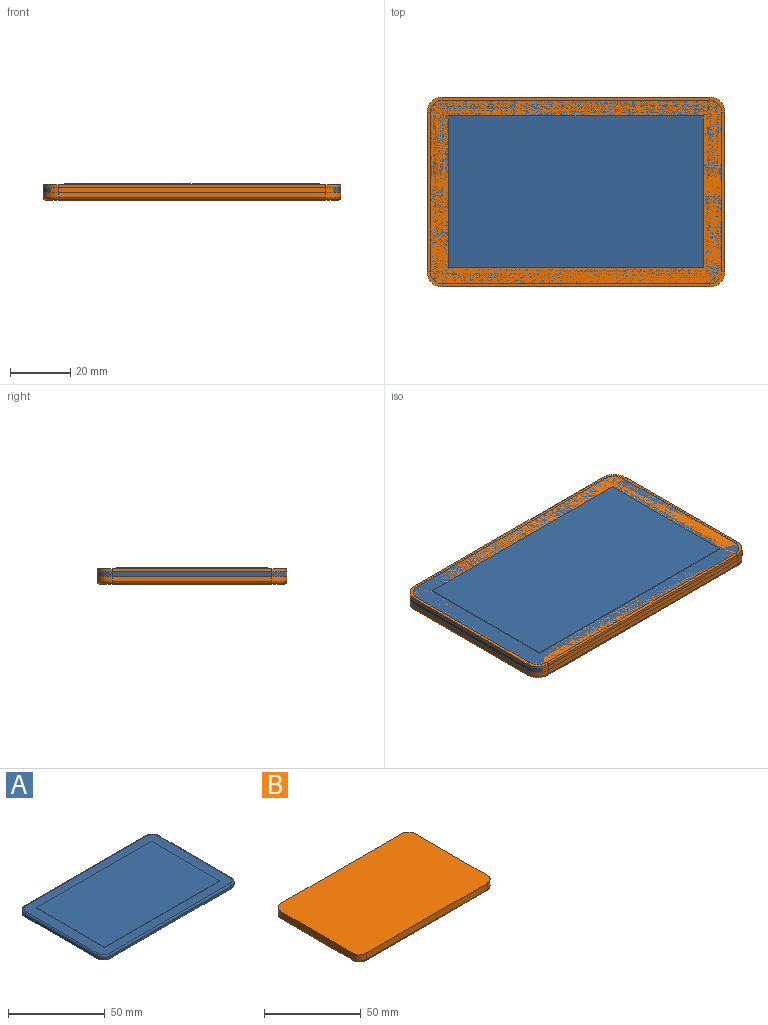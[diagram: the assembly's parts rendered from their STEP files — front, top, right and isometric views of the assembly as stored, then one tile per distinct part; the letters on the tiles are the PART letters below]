
ASSEMBLY  parts=2 mates=1
PART A: 23 faces, bbox 99.3x63.6x2.8 mm
  f0: plane 96.5x60.76mm, normal (0,0,1), area 1613.6mm2, adj f6,f7,f8,f9,f11,f13,f15,f17
  f1: plane 88.34x1.54mm, normal (0,1,0), area 136mm2, adj f5,f6,f14,f16
  f2: plane 52.6x1.54mm, normal (-1,0,0), area 81mm2, adj f5,f7,f12,f16
  f3: plane 88.34x1.54mm, normal (0,-1,0), area 136mm2, adj f5,f9,f10,f12
  f4: plane 52.6x1.54mm, normal (1,0,0), area 81mm2, adj f5,f8,f10,f14
  f5: plane 98.5x62.76mm, normal (0,0,-1), area 6160.1mm2, adj f1,f2,f3,f4,f10,f12,f14,f16
  f6: cylinder r=1mm len=88.34mm, axis (1,0,0), area 138.8mm2, adj f0,f1,f15,f17
  f7: cylinder r=1mm len=52.6mm, axis (0,1,0), area 82.6mm2, adj f0,f2,f13,f17
  f8: cylinder r=1mm len=52.6mm, axis (0,-1,0), area 82.6mm2, adj f0,f4,f11,f15
  f9: cylinder r=1mm len=88.34mm, axis (-1,0,0), area 138.8mm2, adj f0,f3,f11,f13
  f10: cylinder r=5.08mm len=5.08mm, axis (0,0,1), area 12.3mm2, adj f3,f4,f5,f11
  f11: torus R=4.08mm, axis (0,0,1), area 11.6mm2, adj f0,f8,f9,f10
  f12: cylinder r=5.08mm len=5.08mm, axis (0,0,-1), area 12.3mm2, adj f2,f3,f5,f13
  f13: torus R=4.08mm, axis (0,0,1), area 11.6mm2, adj f0,f7,f9,f12
  f14: cylinder r=5.08mm len=5.08mm, axis (0,0,-1), area 12.3mm2, adj f1,f4,f5,f15
  f15: torus R=4.08mm, axis (0,0,1), area 11.6mm2, adj f0,f6,f8,f14
  f16: cylinder r=5.08mm len=5.08mm, axis (0,0,1), area 12.3mm2, adj f1,f2,f5,f17
  f17: torus R=4.08mm, axis (0,0,1), area 11.6mm2, adj f0,f6,f7,f16
  f18: plane 84.26x0.25mm, normal (0,1,0), area 21.4mm2, adj f0,f19,f21,f22
  f19: plane 50.27x0.25mm, normal (-1,0,0), area 12.8mm2, adj f0,f18,f20,f22
  f20: plane 84.26x0.25mm, normal (0,-1,0), area 21.4mm2, adj f0,f19,f21,f22
  f21: plane 50.27x0.25mm, normal (1,0,0), area 12.8mm2, adj f0,f18,f20,f22
  f22: plane 84.26x50.27mm, normal (0,0,1), area 4235.8mm2, adj f18,f19,f20,f21
PART B: 18 faces, bbox 99.3x63.6x5.1 mm
  f0: plane 96.5x60.77mm, normal (0,0,-1), area 5849.4mm2, adj f6,f7,f8,f9,f11,f13,f15,f17
  f1: plane 88.34x4.08mm, normal (0,1,0), area 360.4mm2, adj f5,f6,f14,f16
  f2: plane 52.61x4.08mm, normal (-1,0,0), area 214.6mm2, adj f5,f7,f12,f16
  f3: plane 88.34x4.08mm, normal (0,-1,0), area 360.4mm2, adj f5,f9,f10,f12
  f4: plane 52.61x4.08mm, normal (1,0,0), area 214.6mm2, adj f5,f8,f10,f14
  f5: plane 98.5x62.77mm, normal (0,0,1), area 6160.1mm2, adj f1,f2,f3,f4,f10,f12,f14,f16
  f6: cylinder r=1mm len=88.34mm, axis (1,0,0), area 138.8mm2, adj f0,f1,f15,f17
  f7: cylinder r=1mm len=52.61mm, axis (0,1,0), area 82.6mm2, adj f0,f2,f13,f17
  f8: cylinder r=1mm len=52.61mm, axis (0,-1,0), area 82.6mm2, adj f0,f4,f11,f15
  f9: cylinder r=1mm len=88.34mm, axis (-1,0,0), area 138.8mm2, adj f0,f3,f11,f13
  f10: cylinder r=5.08mm len=5.08mm, axis (0,0,-1), area 32.6mm2, adj f3,f4,f5,f11
  f11: torus R=4.08mm, axis (0,0,1), area 11.6mm2, adj f0,f8,f9,f10
  f12: cylinder r=5.08mm len=5.08mm, axis (0,0,1), area 32.6mm2, adj f2,f3,f5,f13
  f13: torus R=4.08mm, axis (0,0,1), area 11.6mm2, adj f0,f7,f9,f12
  f14: cylinder r=5.08mm len=5.08mm, axis (0,0,1), area 32.6mm2, adj f1,f4,f5,f15
  f15: torus R=4.08mm, axis (0,0,1), area 11.6mm2, adj f0,f6,f8,f14
  f16: cylinder r=5.08mm len=5.08mm, axis (0,0,-1), area 32.6mm2, adj f1,f2,f5,f17
  f17: torus R=4.08mm, axis (0,0,1), area 11.6mm2, adj f0,f6,f7,f16
PLACE A t=(-0.91,0.15,-2.78)mm
PLACE B t=(-0.91,0.15,-0.24)mm
MATE slider B.f5 <-> A.f0  axis (0,0,1) through (-0.91,0.15,-0.24)mm
